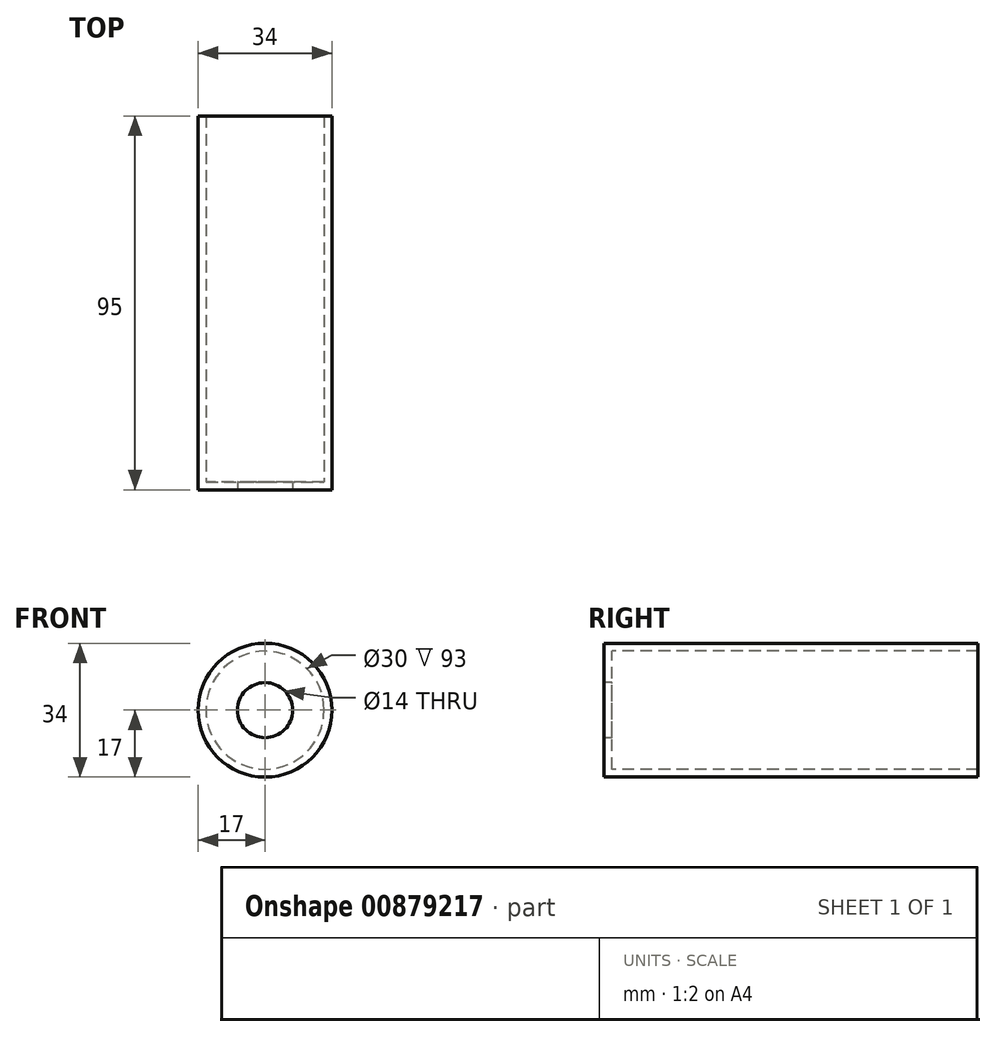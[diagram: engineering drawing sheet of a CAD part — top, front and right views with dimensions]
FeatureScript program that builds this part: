
annotation { "Feature Type Name" : "Feature", "Feature Type Description" : "" }
export const myFeature = defineFeature(function(context is Context, id is Id, definition is map)
    precondition{}
    {
        {
            var Q0;
            Q0=qCreatedBy(makeId("Front.planeOp"),FACE);
            var sketch = newSketch(context, id + "F0", { "sketchPlane" : qUnion([Q0])});
            skCircle(sketch, "E0", {"center": v(0, 0) * mm, "radius": 7 * mm});
            skPoint(sketch, "E1", {"position": v(-5.52, 4.3) * mm});
            skCircle(sketch, "E2", {"center": v(0, 0) * mm, "radius": 17 * mm});
            skPoint(sketch, "E3", {"position": v(-7.36, 15.33) * mm});
            skCircle(sketch, "E4", {"center": v(0, 0) * mm, "radius": 15 * mm});
            skPoint(sketch, "E5", {"position": v(10.27, 10.94) * mm});
            skSolve(sketch);
        }
        {
            var Q0;
            Q0 = qSketchRegion(id + "F0", true);
            extrude(context, id + "F1", {"entities" : qUnion([Q0]), "oppositeDirection" : true, "depth" : 95 * mm, "offsetDistance" : 25 * mm});
        }
        {
            var Q0;
            Q0=makeQuery(id+"F0.imprint","IMPRINT",FACE,{"disambiguationData":[TD([[makeQuery(id+"F0.imprint","IMPRINT",EDGE,{"derivedFrom":sQuery(id+"F0.wireOp",EDGE,"E0")}),-1.0]])]});
            extrude(context, id + "F2", {"entities" : qUnion([Q0]), "operationType" : NewBodyOperationType.ADD, "oppositeDirection" : true, "depth" : 2 * mm, "offsetDistance" : 25 * mm});
        }
    });
